# Revit family: Haworth_Bac_Table_Rectangle
name_source: partatom
category: Furniture
revit_build: Autodesk Revit 2018 (Build: 20170223_1515(x64)
units: mm (PartAtom-declared; Revit-internal decimal feet)

## family parameters
Always vertical = Yes
Cut with Voids When Loaded = No
OmniClass Number = 23.40.70.14.64.21
OmniClass Title = Systems Furniture
Room Calculation Point = No
Shared = No
Work Plane-Based = No

## types (2) — shared parameters
Actual Depth = 33 1/2"
Actual Height = 29"
Assembly Code = E2020200
Leg Depth = 3 15/16"
Manufacturer = Haworth
Revision Number = 4
Size = Verify Final Dim. w/ Haworth
Standard Depths = 33.5 in.
Standard Height = 29 in.
Standard Widths = 79 in. or 94.5 in.
Support Depth = 2 93/256"
Support Height = 4 43/256"
Support Offset = 8"
Table Thickness = 1"
URL = http://www.haworth.com
URL - Product = https://www.haworth.com
Warranty = http://www.haworth.com

## per-type parameters (varying)
| type | Actual Width | Description | Large | Model | Small |
| HCCE-BCTS - 33d 79w | 79" | Haworth Bac Table Rectangle - 33d 79w | No | HCCE-BCTS | Yes |
| HCCE-BCTL - 33d 94w | 94 1/2" | Haworth Bac Table Rectangle - 33d 94w | Yes | HCCE-BCTL-L | No |

## geometry (parser evidence)
native form markers: Sweep x2
no freeform markers — native parametric forms only
